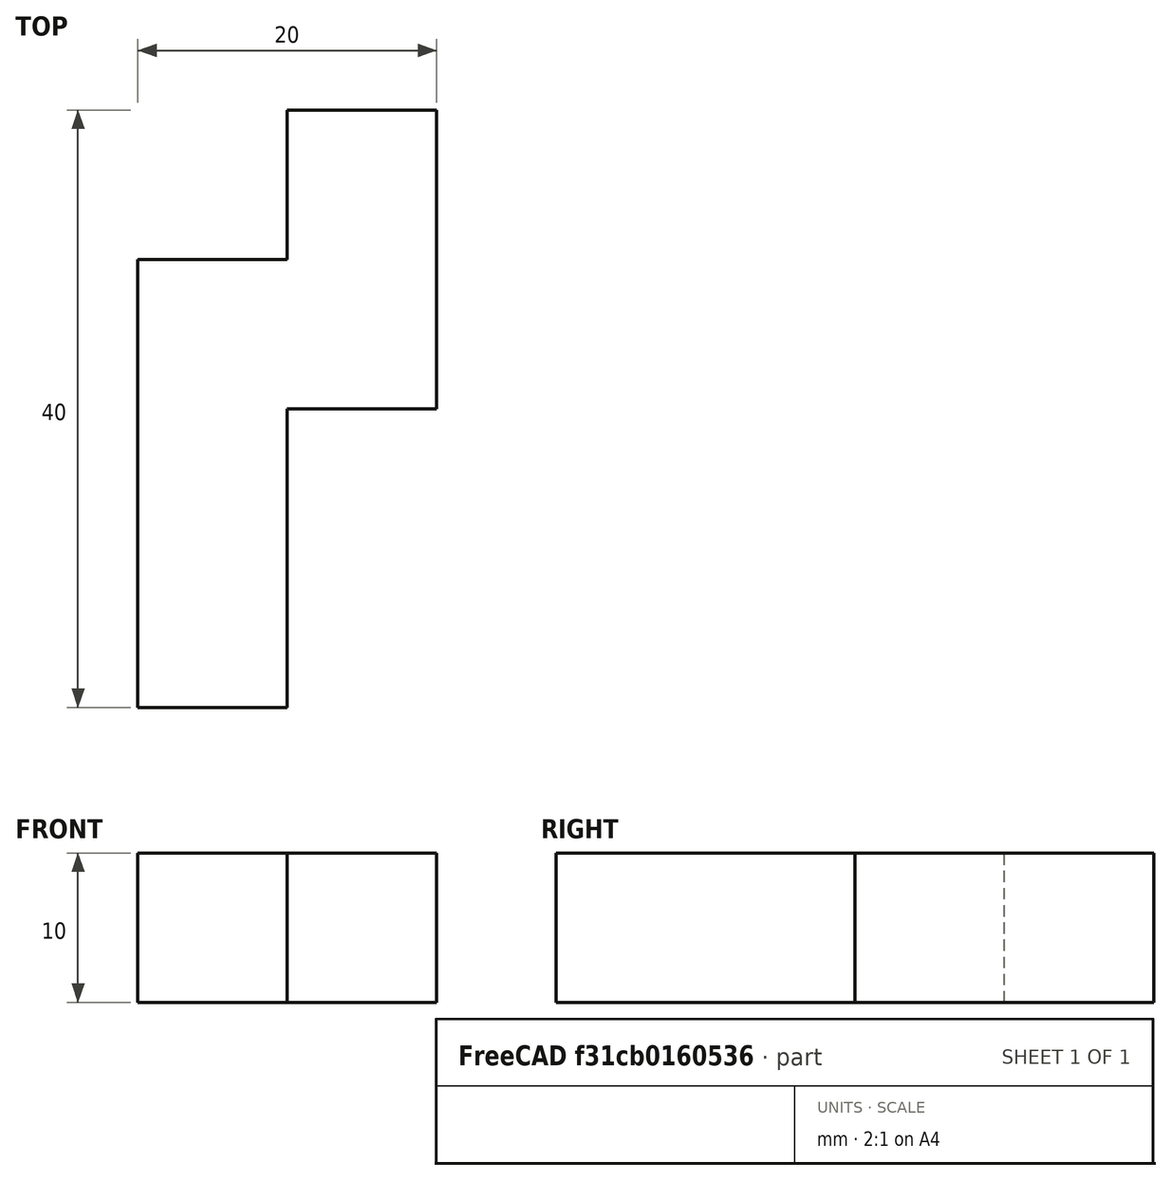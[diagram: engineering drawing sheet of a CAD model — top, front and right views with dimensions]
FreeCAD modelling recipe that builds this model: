
FCSTD DOCUMENT  (FreeCAD 0.16R)
Label: N
License: All rights reserved
LicenseURL: http://en.wikipedia.org/wiki/All_rights_reserved
objects: Sketcher::SketchObject×1, PartDesign::Pad×1
note: 3 computed .brp shape members not serialized (recipe doc carries the construction recipe); baked Part::Feature solids carry a one-line shape summary decoded from their .brp

FEATURE [Sketcher::SketchObject] Sketch
  sketch-geometry (8):
    g0: LineSegment StartX=17.3173 StartY=37.6569 StartZ=0 EndX=27.3173 EndY=37.6569 EndZ=0
    g1: LineSegment StartX=27.3173 StartY=37.6569 StartZ=0 EndX=27.3173 EndY=47.6569 EndZ=0
    g2: LineSegment StartX=27.3173 StartY=47.6569 StartZ=0 EndX=37.3173 EndY=47.6569 EndZ=0
    g3: LineSegment StartX=37.3173 StartY=47.6569 StartZ=0 EndX=37.3173 EndY=27.6569 EndZ=0
    g4: LineSegment StartX=37.3173 StartY=27.6569 StartZ=0 EndX=27.3173 EndY=27.6569 EndZ=0
    g5: LineSegment StartX=27.3173 StartY=27.6569 StartZ=0 EndX=27.3173 EndY=7.65692 EndZ=0
    g6: LineSegment StartX=27.3173 StartY=7.65692 StartZ=0 EndX=17.3173 EndY=7.65692 EndZ=0
    g7: LineSegment StartX=17.3173 StartY=37.6569 StartZ=0 EndX=17.3173 EndY=7.65692 EndZ=0
  constraints (25):
    c: Horizontal(g0)
    c: Coincident(g0,g1)
    c: Vertical(g1)
    c: Coincident(g1,g2)
    c: Coincident(g2,g3)
    c: Coincident(g3,g4)
    c: Coincident(g4,g5)
    c: Vertical(g5)
    c: Coincident(g5,g6)
    c: Coincident(g0,g7)
    c: PointOnObject(g7,g6)
    c: Vertical(g7)
    c: Coincident(g7,g6)
    c: Distance(g0) = 10
    c: Distance(g1) = 10
    c: Distance(g2) = 10
    c: Distance(g3) = 20
    c: Distance(g4) = 10
    c: Distance(g5) = 20
    c: Distance(g7) = 30
    c: Distance(g6) = 10
    c: Horizontal(g2)
    c: DistanceX(g6) = 17.3173
    c: DistanceY(g6) = 7.65692
    c: Perpendicular(g5,g4)
FEATURE [PartDesign::Pad] Pad
  Length = 10
  Length2 = 100
  Sketch = -> Sketch
  Type = 0
